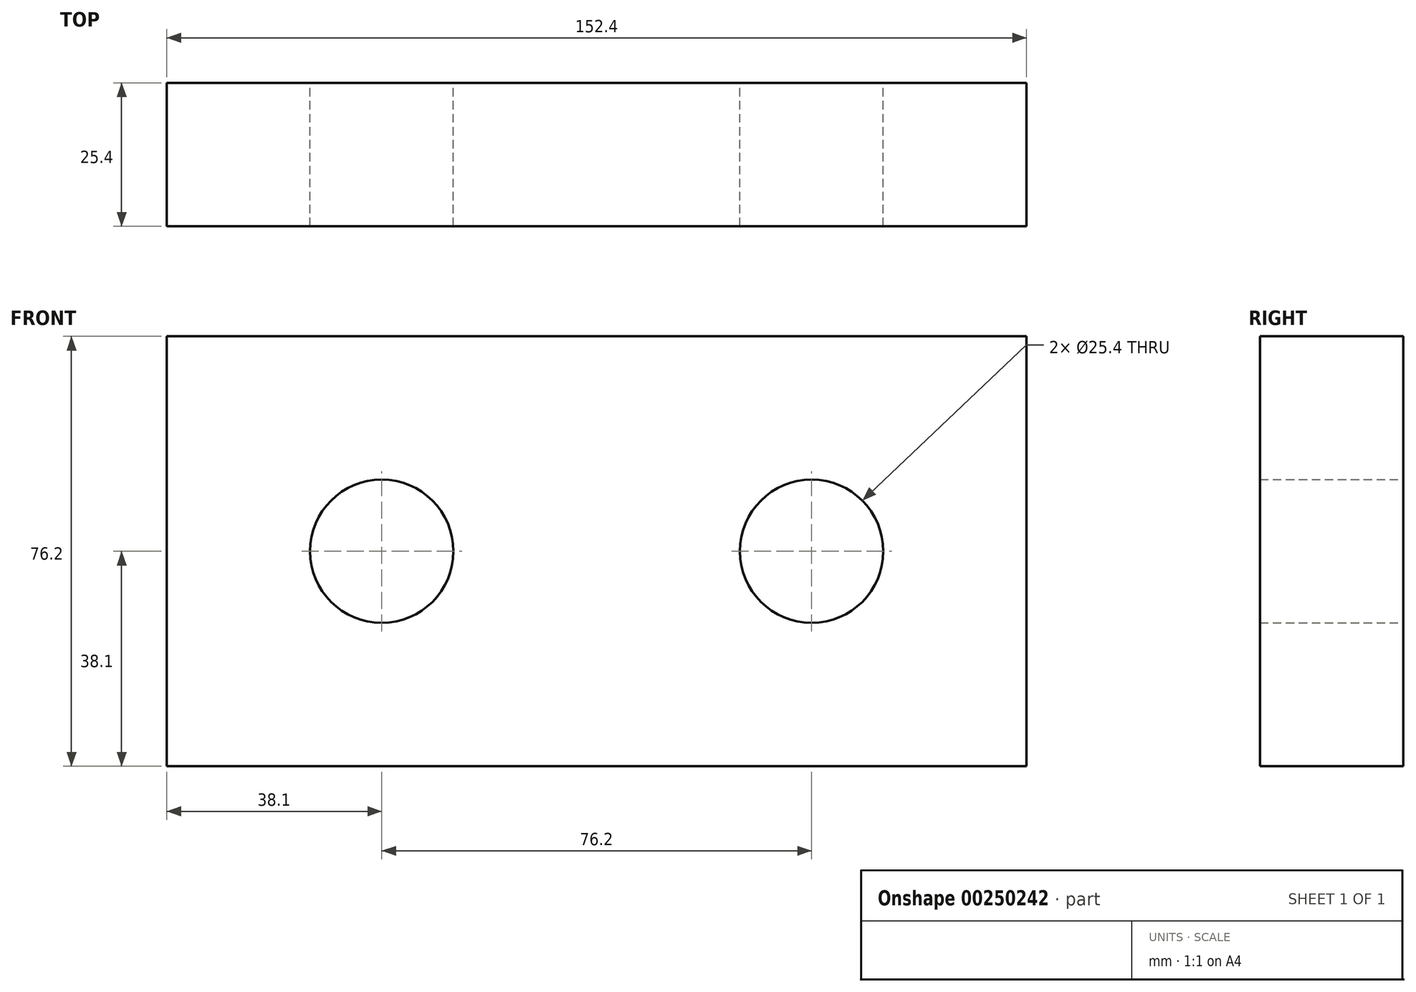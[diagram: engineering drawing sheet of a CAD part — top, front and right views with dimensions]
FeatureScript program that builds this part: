
annotation { "Feature Type Name" : "Feature", "Feature Type Description" : "" }
export const myFeature = defineFeature(function(context is Context, id is Id, definition is map)
    precondition{}
    {
        {
            var Q0;
            Q0=qCreatedBy(makeId("Front.planeOp"),FACE);
            var sketch = newSketch(context, id + "F0", { "sketchPlane" : qUnion([Q0])});
            skLineSegment(sketch, "E0.bottom", {"start": v(76.2, -38.1) * mm, "end": v(-76.2, -38.1) * mm});
            skLineSegment(sketch, "E0.top", {"start": v(76.2, 38.1) * mm, "end": v(-76.2, 38.1) * mm});
            skLineSegment(sketch, "E0.left", {"start": v(76.2, -38.1) * mm, "end": v(76.2, 38.1) * mm});
            skLineSegment(sketch, "E0.right", {"start": v(-76.2, -38.1) * mm, "end": v(-76.2, 38.1) * mm});
            skPoint(sketch, "E0.middle", {"position": v(0, 0) * mm});
            skCircle(sketch, "E1", {"center": v(-38.1, 0) * mm, "radius": 12.7 * mm});
            skCircle(sketch, "E2", {"center": v(38.1, 0) * mm, "radius": 12.7 * mm});
            skSolve(sketch);
        }
        {
            var Q0;
            Q0=makeQuery(id+"F0.imprint","IMPRINT",FACE,{"disambiguationData":[TD([[makeQuery(id+"F0.imprint","IMPRINT",EDGE,{"derivedFrom":sQuery(id+"F0.wireOp",EDGE,"E0.bottom")}),-1.0]])]});
            extrude(context, id + "F1", {"entities" : qUnion([Q0]), "depth" : 25.4 * mm});
        }
    });
